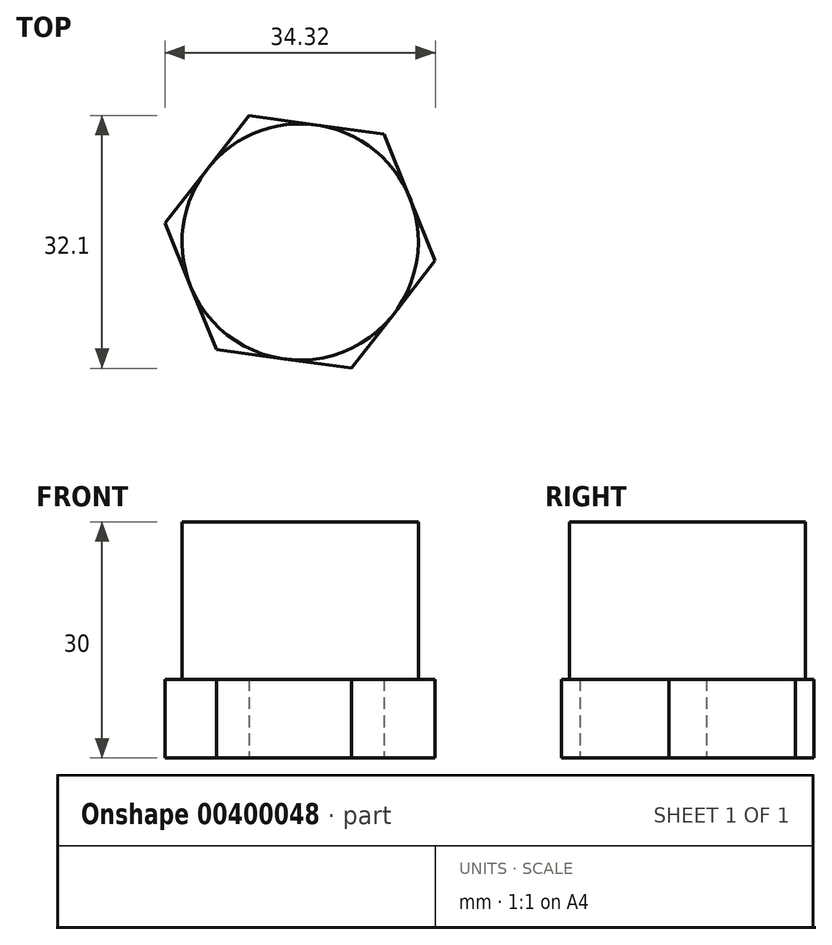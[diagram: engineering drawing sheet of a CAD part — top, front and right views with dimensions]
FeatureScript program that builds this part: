
annotation { "Feature Type Name" : "Feature", "Feature Type Description" : "" }
export const myFeature = defineFeature(function(context is Context, id is Id, definition is map)
    precondition{}
    {
        {
            var Q0;
            Q0=qCreatedBy(makeId("Top.planeOp"),FACE);
            var sketch = newSketch(context, id + "F0", { "sketchPlane" : qUnion([Q0])});
            skCircle(sketch, "E0", {"center": v(0, 0) * mm, "radius": 15 * mm});
            skCircle(sketch, "E1.cCircle", {"center": v(0, 0) * mm, "radius": 15 * mm, "construction": true});
            skLineSegment(sketch, "E1.0", {"start": v(-6.52, 16.05) * mm, "end": v(10.63, 13.67) * mm});
            skLineSegment(sketch, "E1.1", {"start": v(10.63, 13.67) * mm, "end": v(17.16, -2.37) * mm});
            skLineSegment(sketch, "E1.2", {"start": v(17.16, -2.37) * mm, "end": v(6.52, -16.05) * mm});
            skLineSegment(sketch, "E1.3", {"start": v(6.52, -16.05) * mm, "end": v(-10.63, -13.67) * mm});
            skLineSegment(sketch, "E1.4", {"start": v(-10.63, -13.67) * mm, "end": v(-17.16, 2.37) * mm});
            skLineSegment(sketch, "E1.5", {"start": v(-17.16, 2.37) * mm, "end": v(-6.52, 16.05) * mm});
            skPoint(sketch, "E1.0.midPoint", {"position": v(2.06, 14.86) * mm});
            skSolve(sketch);
        }
        {
            var Q0;
            {var subQ0=sQuery(id+"F0.wireOp",EDGE,"E0");var subQ4=makeQuery(id+"F0.imprint","INTERSECT",VERTEX,{"derivedFrom":[subQ0,sQuery(id+"F0.wireOp",EDGE,"E1.0")]});Q0=makeQuery(id+"F0.imprint","IMPRINT",FACE,{"disambiguationData":[TD([[makeQuery(id+"F0.imprint","IMPRINT",EDGE,{"disambiguationData":[TD([[subQ4,1.0]])],"derivedFrom":subQ0}),1.0]])]});}
            extrude(context, id + "F1", {"entities" : qUnion([Q0]), "depth" : 50 * mm});
        }
        {
            var Q0;
            Q0=qSketchRegion(id+"F0",true);
            extrude(context, id + "F2", {"entities" : qUnion([Q0]), "operationType" : NewBodyOperationType.ADD, "depth" : 10 * mm});
        }
        {
            var Q0;
            Q0=makeQuery(id+"F1.opExtrude","CAP_FACE",FACE,{"disambiguationData":[OSD([sQuery(id+"F0.wireOp",EDGE,"E0")])],"isStart":false});
            extrude(context, id + "F3", {"entities" : qUnion([Q0]), "operationType" : NewBodyOperationType.REMOVE, "oppositeDirection" : true, "depth" : 20 * mm});
        }
    });
